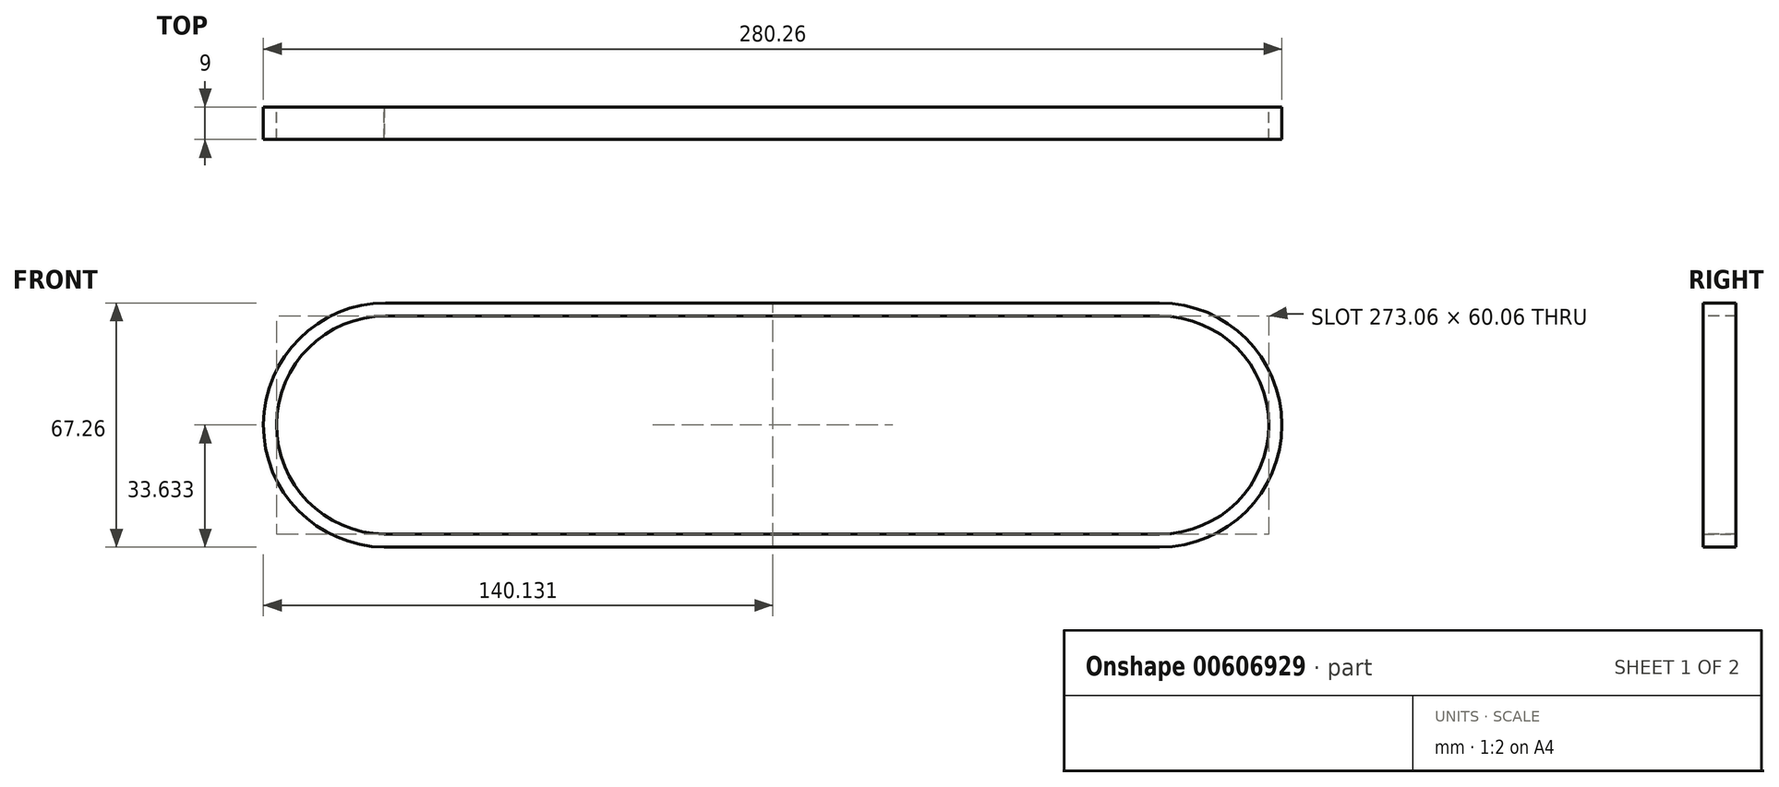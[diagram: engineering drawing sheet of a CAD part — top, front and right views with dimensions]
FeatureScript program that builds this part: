
annotation { "Feature Type Name" : "Feature", "Feature Type Description" : "" }
export const myFeature = defineFeature(function(context is Context, id is Id, definition is map)
    precondition{}
    {
        {
            var Q0;
            Q0=qCreatedBy(makeId("Front.planeOp"),FACE);
            var sketch = newSketch(context, id + "F0", { "sketchPlane" : qUnion([Q0]) });
            skLineSegment(sketch, "E0", {"start": v(114.1, -87.58) * mm, "end": v(114.1, -87.58) * mm});
            skLineSegment(sketch, "E1", {"start": v(-454.19, -603.93) * mm, "end": v(510.81, -603.93) * mm, "construction": true});
            skPoint(sketch, "E2.centerSnap0", {"position": v(28.31, -603.93) * mm});
            skArc(sketch, "E3", {"start": v(-445.32, -634.5) * mm, "mid": v(-422.68, -599.45) * mm, "end": v(-454.19, -572.1) * mm});
            skArc(sketch, "E4", {"start": v(-454.19, -572.1) * mm, "mid": v(-485.7, -608.4) * mm, "end": v(-445.32, -634.5) * mm});
            skArc(sketch, "E5", {"start": v(510.41, -635.75) * mm, "mid": v(542.64, -604.13) * mm, "end": v(510.81, -572.1) * mm});
            skArc(sketch, "E6", {"start": v(510.81, -572.1) * mm, "mid": v(478.98, -603.73) * mm, "end": v(510.41, -635.75) * mm});
            skLineSegment(sketch, "E7", {"start": v(510.81, -572.1) * mm, "end": v(723.81, -572.1) * mm});
            skLineSegment(sketch, "E8", {"start": v(510.41, -635.75) * mm, "end": v(723.81, -635.76) * mm});
            skArc(sketch, "E9", {"start": v(723.81, -635.76) * mm, "mid": v(755.64, -603.93) * mm, "end": v(723.81, -572.1) * mm});
            skSolve(sketch);
        }
        {
            var Q0;
            Q0=sQuery(id+"F0.wireOp",EDGE,"E7");
            cPlane(context, id + "F1", {"entities" : qUnion([Q0]), "cplaneType" : CPlaneType.MID_PLANE, "offset" : 25 * mm, "width" : 150 * mm, "height" : 150 * mm});
        }
        {
            var Q0;
            Q0=qCreatedBy(id+"F1.planeOp",FACE);
            var sketch = newSketch(context, id + "F2", { "sketchPlane" : qUnion([Q0]) });
            skPoint(sketch, "E10.0", {"position": v(0, -572.1) * mm});
            skLineSegment(sketch, "E11.bottom", {"start": v(4.5, -570.3) * mm, "end": v(-4.5, -570.3) * mm});
            skLineSegment(sketch, "E11.top", {"start": v(4.5, -573.9) * mm, "end": v(-4.5, -573.9) * mm});
            skLineSegment(sketch, "E11.left", {"start": v(4.5, -570.3) * mm, "end": v(4.5, -573.9) * mm});
            skLineSegment(sketch, "E11.right", {"start": v(-4.5, -570.3) * mm, "end": v(-4.5, -573.9) * mm});
            skSolve(sketch);
        }
        {
            var Q0;
            Q0=makeQuery(id+"F2.imprint","IMPRINT",FACE,{"disambiguationData":[TD([[makeQuery(id+"F2.imprint","IMPRINT",EDGE,{"derivedFrom":sQuery(id+"F2.wireOp",EDGE,"E11.bottom")}),1.0]])]});
            var Q1;
            Q1=sQuery(id+"F0.wireOp",EDGE,"E7");
            var Q2;
            Q2=sQuery(id+"F0.wireOp",EDGE,"E9");
            var Q3;
            Q3=sQuery(id+"F0.wireOp",EDGE,"E8");
            var Q4;
            Q4=sQuery(id+"F0.wireOp",EDGE,"E6");
            sweep(context, id + "F3", {"profiles" : qUnion([Q0]), "path" : qUnion([Q1, Q2, Q3, Q4])});
        }
    });
